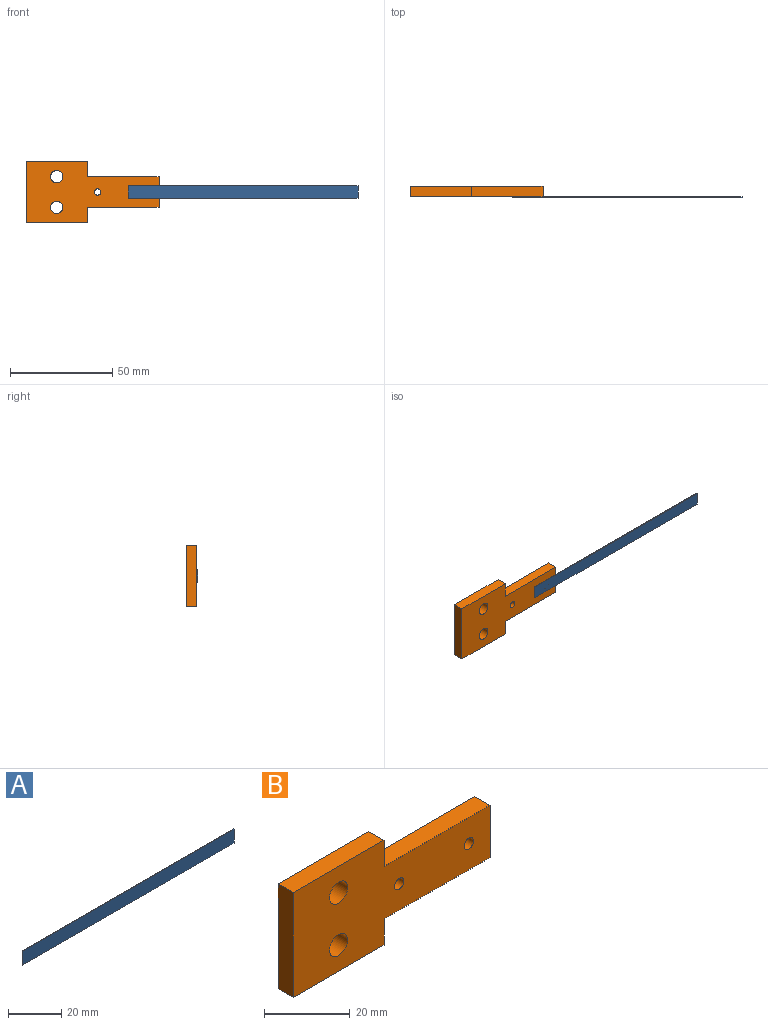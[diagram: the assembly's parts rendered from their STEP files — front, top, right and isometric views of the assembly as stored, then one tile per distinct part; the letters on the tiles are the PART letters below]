
ASSEMBLY  parts=2 mates=3
PART A: 6 faces, bbox 112.2x0.4x6.4 mm
  f0: plane 112.24x0.43mm, normal (0,0,1), area 48.3mm2, adj f1,f3,f4,f5
  f1: plane 6.35x0.43mm, normal (-1,0,0), area 2.7mm2, adj f0,f2,f4,f5
  f2: plane 112.24x0.43mm, normal (0,0,-1), area 48.3mm2, adj f1,f3,f4,f5
  f3: plane 6.35x0.43mm, normal (1,0,0), area 2.7mm2, adj f0,f2,f4,f5
  f4: plane 112.24x6.35mm, normal (0,-1,0), area 712.7mm2, adj f0,f1,f2,f3
  f5: plane 112.24x6.35mm, normal (0,1,0), area 712.7mm2, adj f0,f1,f2,f3
PART B: 14 faces, bbox 65x5x30 mm
  f0: plane 30x5mm, normal (0,0,1), area 150mm2, adj f1,f11,f12,f13
  f1: plane 30x5mm, normal (-1,0,0), area 150mm2, adj f0,f2,f12,f13
  f2: plane 30x5mm, normal (0,0,-1), area 150mm2, adj f1,f3,f12,f13
  f3: plane 7.5x5mm, normal (1,0,0), area 37.5mm2, adj f2,f4,f12,f13
  f4: plane 35x5mm, normal (0,0,-1), area 175mm2, adj f3,f5,f12,f13
  f5: plane 15x5mm, normal (1,0,0), area 75mm2, adj f4,f6,f12,f13
  f6: plane 35x5mm, normal (0,0,1), area 175mm2, adj f5,f11,f12,f13
  f7: cylinder r=3mm len=6mm, axis (0,1,0), area 94.2mm2, adj f12,f13
  f8: cylinder r=3mm len=6mm, axis (0,1,0), area 94.2mm2, adj f12,f13
  f9: cylinder r=1.55mm len=5mm, axis (0,1,0), area 48.7mm2, adj f12,f13
  f10: cylinder r=1.55mm len=5mm, axis (0,1,0), area 48.7mm2, adj f12,f13
  f11: plane 7.5x5mm, normal (1,0,0), area 37.5mm2, adj f0,f6,f12,f13
  f12: plane 65x30mm, normal (0,-1,0), area 1353.4mm2, adj f0,f1,f2,f3,f4,f5,f6,f7
  f13: plane 65x30mm, normal (0,1,0), area 1353.4mm2, adj f0,f1,f2,f3,f4,f5,f6,f7
PLACE A t=(50,0,18.17)mm
PLACE B t=(0,5,15)mm
MATE slider B.f5 <-> A.f1  axis (1,0,0) through (65,0,15)mm
MATE parallel A.f1 <-> B.f5  axis (-1,0,0) through (50,-0.21,15)mm
MATE planar A.f5 <-> B.f12  axis (0,1,0) through (106.12,0,15)mm
